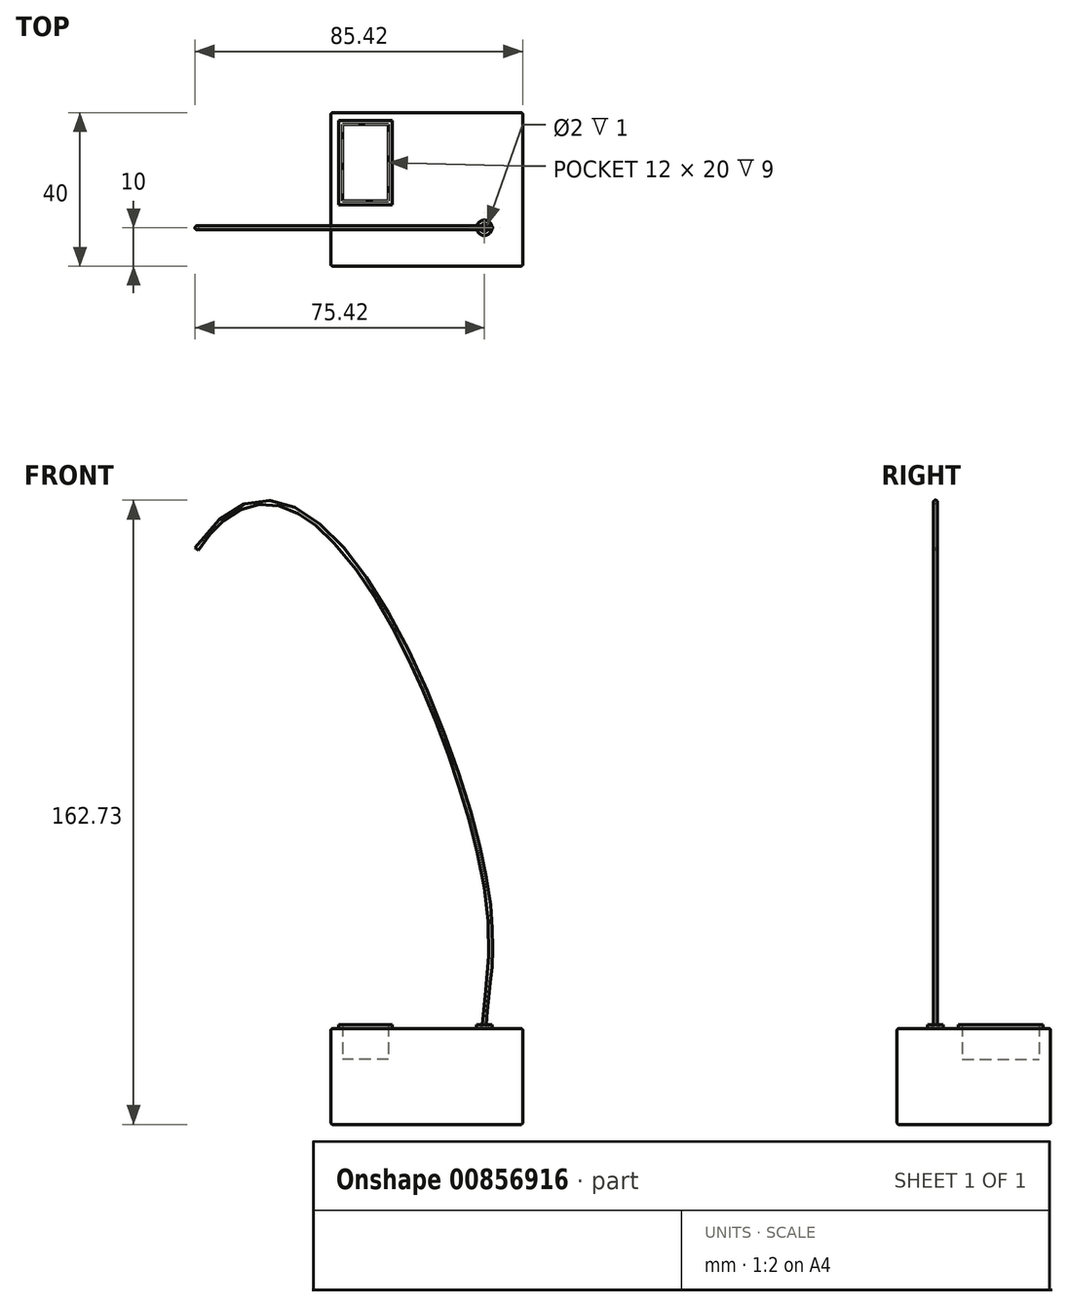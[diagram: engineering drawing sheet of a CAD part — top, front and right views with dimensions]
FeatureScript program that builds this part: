
annotation { "Feature Type Name" : "Feature", "Feature Type Description" : "" }
export const myFeature = defineFeature(function(context is Context, id is Id, definition is map)
    precondition{}
    {
        {
            var Q0;
            Q0=qCreatedBy(makeId("Top.planeOp"),FACE);
            var sketch = newSketch(context, id + "F0", { "sketchPlane" : qUnion([Q0])});
            skLineSegment(sketch, "E0.bottom", {"start": v(25, -20) * mm, "end": v(-25, -20) * mm});
            skLineSegment(sketch, "E0.top", {"start": v(25, 20) * mm, "end": v(-25, 20) * mm});
            skLineSegment(sketch, "E0.left", {"start": v(25, -20) * mm, "end": v(25, 20) * mm});
            skLineSegment(sketch, "E0.right", {"start": v(-25, -20) * mm, "end": v(-25, 20) * mm});
            skPoint(sketch, "E0.middle", {"position": v(0, 0) * mm});
            skSolve(sketch);
        }
        {
            var Q0;
            Q0=makeQuery(id+"F0.imprint","IMPRINT",FACE,{"disambiguationData":[TD([[makeQuery(id+"F0.imprint","IMPRINT",EDGE,{"derivedFrom":sQuery(id+"F0.wireOp",EDGE,"E0.bottom")}),-1.0]])]});
            extrude(context, id + "F1", {"entities" : qUnion([Q0]), "depth" : 25 * mm, "offsetDistance" : 25 * mm});
        }
        {
            var Q0;
            Q0=makeQuery(id+"F1.opExtrude","CAP_FACE",FACE,{"disambiguationData":[OSD([sQuery(id+"F0.wireOp",EDGE,"E0.bottom"),sQuery(id+"F0.wireOp",EDGE,"E0.top"),sQuery(id+"F0.wireOp",EDGE,"E0.left"),sQuery(id+"F0.wireOp",EDGE,"E0.right")])],"isStart":false});
            var sketch = newSketch(context, id + "F2", { "sketchPlane" : qUnion([Q0])});
            skLineSegment(sketch, "E1.bottom", {"start": v(-9, 18) * mm, "end": v(-23, 18) * mm});
            skLineSegment(sketch, "E1.top", {"start": v(-9, -4) * mm, "end": v(-23, -4) * mm});
            skLineSegment(sketch, "E1.left", {"start": v(-9, 18) * mm, "end": v(-9, -4) * mm});
            skLineSegment(sketch, "E1.right", {"start": v(-23, 18) * mm, "end": v(-23, -4) * mm});
            skPoint(sketch, "E1.middle", {"position": v(-16, 7) * mm});
            skLineSegment(sketch, "E2.bottom", {"start": v(-10, -3) * mm, "end": v(-22, -3) * mm});
            skLineSegment(sketch, "E2.top", {"start": v(-10, 17) * mm, "end": v(-22, 17) * mm});
            skLineSegment(sketch, "E2.left", {"start": v(-10, -3) * mm, "end": v(-10, 17) * mm});
            skLineSegment(sketch, "E2.right", {"start": v(-22, -3) * mm, "end": v(-22, 17) * mm});
            skCircle(sketch, "E3", {"center": v(15, -10) * mm, "radius": 2 * mm});
            skCircle(sketch, "E4", {"center": v(15, -10) * mm, "radius": 1 * mm});
            skSolve(sketch);
        }
        {
            var Q0;
            Q0 = qSketchRegion(id + "F2", true);
            extrude(context, id + "F3", {"entities" : qUnion([Q0]), "operationType" : NewBodyOperationType.ADD, "depth" : 1 * mm, "offsetDistance" : 25 * mm});
        }
        {
            var Q0;
            Q0=makeQuery(id+"F3.boolean.opBoolean","SPLIT",FACE,{"disambiguationData":[TD([makeQuery(id+"F3.opExtrude","SWEPT_FACE",FACE,{"disambiguationData":[OSD([sQuery(id+"F2.wireOp",EDGE,"E2.bottom")])]})])],"derivedFrom":makeQuery(id+"F1.opExtrude","CAP_FACE",FACE,{"disambiguationData":[OSD([sQuery(id+"F0.wireOp",EDGE,"E0.bottom"),sQuery(id+"F0.wireOp",EDGE,"E0.top"),sQuery(id+"F0.wireOp",EDGE,"E0.left"),sQuery(id+"F0.wireOp",EDGE,"E0.right")])],"isStart":false})});
            extrude(context, id + "F4", {"entities" : qUnion([Q0]), "operationType" : NewBodyOperationType.REMOVE, "oppositeDirection" : true, "depth" : 8 * mm, "offsetDistance" : 25 * mm});
        }
        {
            var Q0;
            Q0=makeQuery(id+"F1.opExtrude","SWEPT_FACE",FACE,{"disambiguationData":[OSD([sQuery(id+"F0.wireOp",EDGE,"E0.bottom")])]});
            cPlane(context, id + "F5", {"entities" : qUnion([Q0]), "cplaneType" : CPlaneType.OFFSET, "offset" : 10 * mm, "oppositeDirection" : true, "width" : 150 * mm, "height" : 150 * mm});
        }
        {
            var Q0;
            Q0=qCreatedBy(id+"F5.planeOp",FACE);
            var sketch = newSketch(context, id + "F6", { "sketchPlane" : qUnion([Q0])});
            skLineSegment(sketch, "E5.0", {"start": v(13, 25) * mm, "end": v(17, 25) * mm, "construction": true});
            skFitSpline(sketch, "E6", {"points": [v(15, 25) * mm, v(13.23, 72.74) * mm, v(-60, 150) * mm], "startDerivative": vector(0, 83.51) * mm, "endDerivative": vector(-143.19, -213.8) * mm});
            skLineSegment(sketch, "E7", {"start": v(15, 25) * mm, "end": v(15, 12.73) * mm, "construction": true});
            skSolve(sketch);
        }
        {
            var Q0;
            {var subQ0=sQuery(id+"F0.wireOp",EDGE,"E0.left");var subQ1=sQuery(id+"F0.wireOp",EDGE,"E0.top");var subQ2=sQuery(id+"F0.wireOp",EDGE,"E0.right");var subQ3=sQuery(id+"F0.wireOp",EDGE,"E0.bottom");Q0=makeQuery(id+"F3.boolean.opBoolean","SPLIT",FACE,{"disambiguationData":[TD([makeQuery(id+"F1.opExtrude","SWEPT_FACE",FACE,{"disambiguationData":[OSD([subQ3])]})])],"derivedFrom":makeQuery(id+"F1.opExtrude","CAP_FACE",FACE,{"disambiguationData":[OSD([subQ3,subQ1,subQ0,subQ2])],"isStart":false})});}
            var sketch = newSketch(context, id + "F7", { "sketchPlane" : qUnion([Q0])});
            skCircle(sketch, "E8", {"center": v(15, -10) * mm, "radius": 0.5 * mm});
            skSolve(sketch);
        }
        {
            var Q0;
            Q0 = qSketchRegion(id + "F7", true);
            var Q1;
            Q1=sQuery(id+"F6.wireOp",EDGE,"E6");
            var Q2;
            Q2=sQuery(id+"F6.wireOp",EDGE,"E6");
            sweep(context, id + "F8", {"operationType" : NewBodyOperationType.ADD, "profiles" : qUnion([Q0]), "surfaceProfiles" : qUnion([Q1]), "path" : qUnion([Q2])});
        }
        {
            var Q0;
            Q0=makeQuery(id+"F1.opExtrude","CAP_EDGE",EDGE,{"disambiguationData":[OSD([sQuery(id+"F0.wireOp",EDGE,"E0.top")])],"isStart":false});
            var Q1;
            Q1=makeQuery(id+"F1.opExtrude","CAP_EDGE",EDGE,{"disambiguationData":[OSD([sQuery(id+"F0.wireOp",EDGE,"E0.left")])],"isStart":false});
            var Q2;
            Q2=makeQuery(id+"F1.opExtrude","CAP_EDGE",EDGE,{"disambiguationData":[OSD([sQuery(id+"F0.wireOp",EDGE,"E0.bottom")])],"isStart":false});
            var Q3;
            Q3=makeQuery(id+"F1.opExtrude","CAP_EDGE",EDGE,{"disambiguationData":[OSD([sQuery(id+"F0.wireOp",EDGE,"E0.right")])],"isStart":false});
            var Q4;
            Q4=makeQuery(id+"F1.opExtrude","SWEPT_EDGE",EDGE,{"disambiguationData":[OSD([sQuery(id+"F0.wireOp",EDGE,"E0.top"),sQuery(id+"F0.wireOp",EDGE,"E0.right")])]});
            var Q5;
            Q5=makeQuery(id+"F1.opExtrude","SWEPT_EDGE",EDGE,{"disambiguationData":[OSD([sQuery(id+"F0.wireOp",EDGE,"E0.top"),sQuery(id+"F0.wireOp",EDGE,"E0.left")])]});
            var Q6;
            Q6=makeQuery(id+"F1.opExtrude","SWEPT_EDGE",EDGE,{"disambiguationData":[OSD([sQuery(id+"F0.wireOp",EDGE,"E0.bottom"),sQuery(id+"F0.wireOp",EDGE,"E0.left")])]});
            var Q7;
            Q7=makeQuery(id+"F1.opExtrude","SWEPT_EDGE",EDGE,{"disambiguationData":[OSD([sQuery(id+"F0.wireOp",EDGE,"E0.bottom"),sQuery(id+"F0.wireOp",EDGE,"E0.right")])]});
            var Q8;
            Q8=makeQuery(id+"F1.opExtrude","CAP_FACE",FACE,{"disambiguationData":[OSD([sQuery(id+"F0.wireOp",EDGE,"E0.bottom"),sQuery(id+"F0.wireOp",EDGE,"E0.top"),sQuery(id+"F0.wireOp",EDGE,"E0.left"),sQuery(id+"F0.wireOp",EDGE,"E0.right")])],"isStart":true});
            fillet(context, id + "F9", {"entities" : qUnion([Q0, Q1, Q2, Q3, Q4, Q5, Q6, Q7, Q8]), "radius" : 0.5 * mm, "tangentPropagation" : true, "allowEdgeOverflow" : false});
        }
    });
